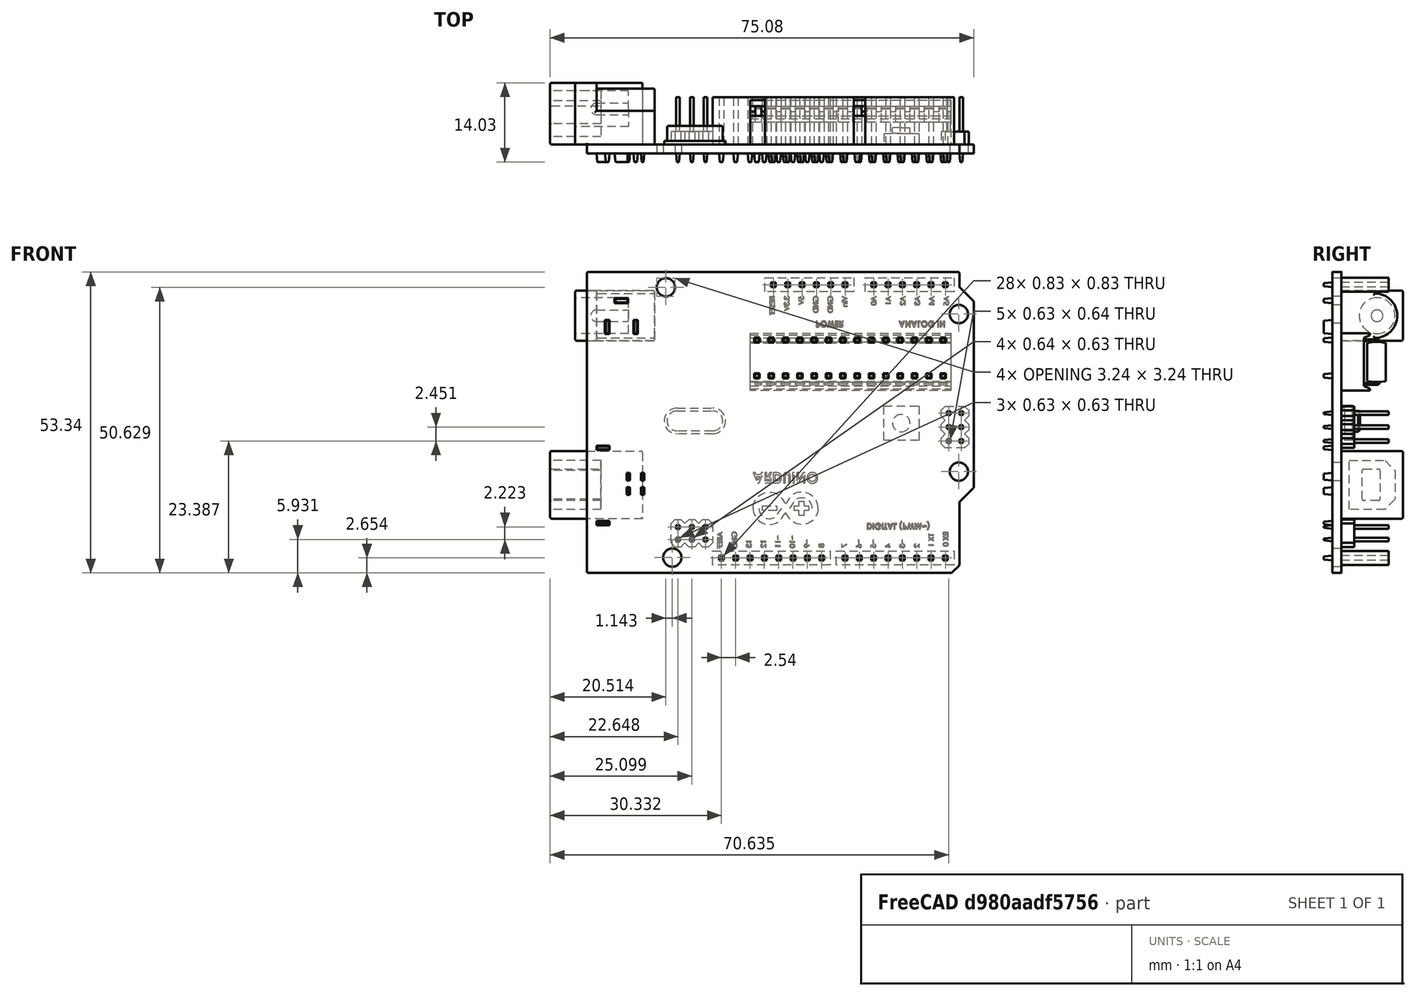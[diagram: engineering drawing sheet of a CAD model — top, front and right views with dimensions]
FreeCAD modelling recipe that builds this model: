
FCSTD DOCUMENT  (FreeCAD 0.18R14555 (Git shallow))
Label: Arduino
License: All rights reserved
LicenseURL: http://en.wikipedia.org/wiki/All_rights_reserved
objects: Part::Feature×1, TechDraw::DrawSVGTemplate×1, TechDraw::DrawPage×1, Part::Part2DObjectPython×1
note: 2 computed .brp shape members not serialized (recipe doc carries the construction recipe); baked Part::Feature solids carry a one-line shape summary decoded from their .brp

FEATURE [Part::Feature] Part__Feature  label="Arduino"
  shape: bbox 75.08 x 14.03 x 53.34 mm, 2276 faces (baked)
FEATURE [TechDraw::DrawSVGTemplate] Template
  EditableTexts = Designed_by_Name=Designed by Name; Drawing_number=Drawing number; FC-Date=Date; FC-SC=Scale; FC-SH=Sheet; FC-Title=Arduino Uni; Subtitle=Subtitle; Weight=Weight
  Height = 210
  Orientation = 1
  Width = 297
FEATURE [TechDraw::DrawPage] Page
  KeepUpdated = true
  ProjectionType = 0
  Template = -> Template
FEATURE [Part::Part2DObjectPython] Shape2DView  # Draft 2D object (typed FeaturePython)
  Base = -> Part__Feature
  HiddenLines = false
  InPlace = true
  Projection = (0,1,0)
  ProjectionMode = 0
  SegmentLength = 0.05
  Tessellation = false
  VisibleOnly = false
